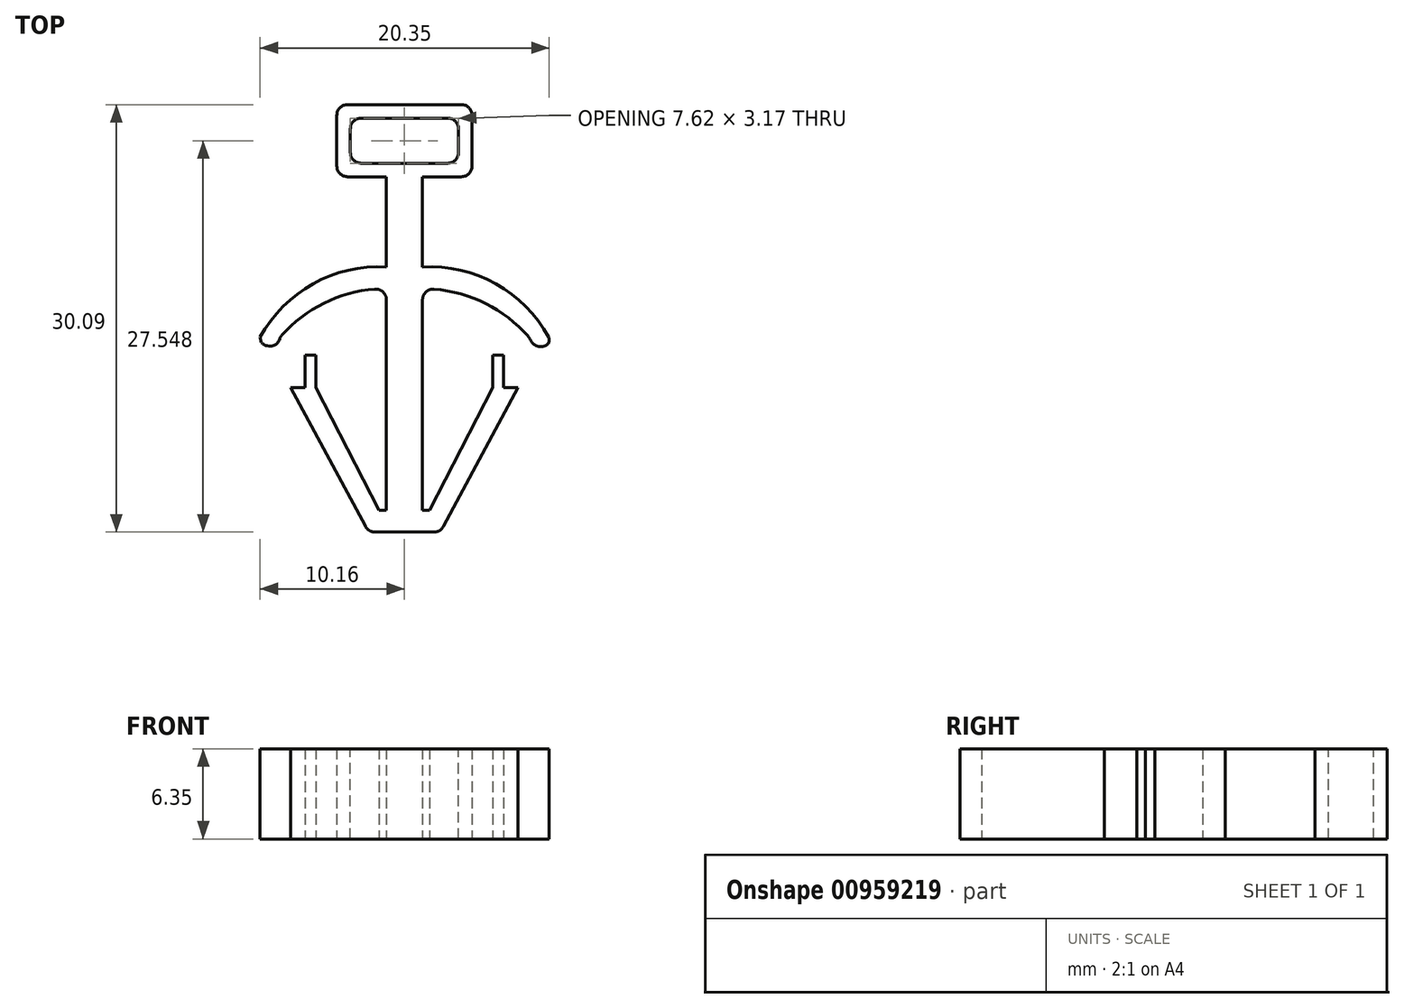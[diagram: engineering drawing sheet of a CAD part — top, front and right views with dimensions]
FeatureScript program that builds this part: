
annotation { "Feature Type Name" : "Feature", "Feature Type Description" : "" }
export const myFeature = defineFeature(function(context is Context, id is Id, definition is map)
    precondition{}
    {
        {
            var Q0;
            Q0=qCreatedBy(makeId("Top.planeOp"),FACE);
            var sketch = newSketch(context, id + "F0", { "sketchPlane" : qUnion([Q0])});
            skLineSegment(sketch, "E0", {"start": v(-4.76, 16.37) * mm, "end": v(4.76, 16.37) * mm});
            skLineSegment(sketch, "E1", {"start": v(4.76, 16.37) * mm, "end": v(4.76, 11.29) * mm});
            skLineSegment(sketch, "E2", {"start": v(4.76, 11.29) * mm, "end": v(1.27, 11.29) * mm});
            skLineSegment(sketch, "E3", {"start": v(1.27, 11.29) * mm, "end": v(1.27, 4.94) * mm});
            skLineSegment(sketch, "E4", {"start": v(-4.76, 16.37) * mm, "end": v(-4.76, 11.29) * mm});
            skLineSegment(sketch, "E5", {"start": v(-4.76, 11.29) * mm, "end": v(-1.27, 11.29) * mm});
            skLineSegment(sketch, "E6", {"start": v(-1.27, 11.29) * mm, "end": v(-1.27, 4.94) * mm});
            skArc(sketch, "E7", {"start": v(10.16, 0) * mm, "mid": v(6.43, 3.75) * mm, "end": v(1.27, 4.94) * mm});
            skArc(sketch, "E8", {"start": v(-1.27, 4.94) * mm, "mid": v(-6.43, 3.75) * mm, "end": v(-10.16, 0) * mm});
            skPoint(sketch, "E9", {"position": v(0, 16.37) * mm});
            skLineSegment(sketch, "E10", {"start": v(-1.8, -4.57) * mm, "end": v(1.8, -4.57) * mm, "construction": true});
            skPoint(sketch, "E11", {"position": v(0, -4.57) * mm});
            skLineSegment(sketch, "E12", {"start": v(-1.27, 11.29) * mm, "end": v(1.27, 11.29) * mm, "construction": true});
            skPoint(sketch, "E13", {"position": v(0, 11.29) * mm});
            skArc(sketch, "E14", {"start": v(-1.27, 3.41) * mm, "mid": v(-5.38, 2.52) * mm, "end": v(-8.75, 0) * mm});
            skArc(sketch, "E15", {"start": v(8.75, 0) * mm, "mid": v(5.38, 2.52) * mm, "end": v(1.27, 3.41) * mm});
            skLineSegment(sketch, "E16", {"start": v(-1.27, 4.94) * mm, "end": v(-1.27, 3.41) * mm, "construction": true});
            skLineSegment(sketch, "E17", {"start": v(-1.27, -12.2) * mm, "end": v(-1.78, -12.2) * mm});
            skLineSegment(sketch, "E18", {"start": v(-1.78, -12.2) * mm, "end": v(-6.22, -3.56) * mm});
            skLineSegment(sketch, "E19", {"start": v(-6.22, -3.56) * mm, "end": v(-6.22, -1.27) * mm});
            skLineSegment(sketch, "E20", {"start": v(-6.22, -1.27) * mm, "end": v(-6.99, -1.27) * mm});
            skLineSegment(sketch, "E21", {"start": v(-6.99, -1.27) * mm, "end": v(-6.99, -3.56) * mm});
            skLineSegment(sketch, "E22", {"start": v(-6.99, -3.56) * mm, "end": v(-8, -3.56) * mm});
            skLineSegment(sketch, "E23", {"start": v(-8, -3.56) * mm, "end": v(-2.54, -13.72) * mm});
            skLineSegment(sketch, "E24", {"start": v(2.54, -13.72) * mm, "end": v(8, -3.56) * mm});
            skLineSegment(sketch, "E25", {"start": v(8, -3.56) * mm, "end": v(6.99, -3.56) * mm});
            skLineSegment(sketch, "E26", {"start": v(6.99, -3.56) * mm, "end": v(6.99, -1.27) * mm});
            skLineSegment(sketch, "E27", {"start": v(6.99, -1.27) * mm, "end": v(6.22, -1.27) * mm});
            skLineSegment(sketch, "E28", {"start": v(1.27, -12.2) * mm, "end": v(1.27, 3.41) * mm});
            skLineSegment(sketch, "E29", {"start": v(6.22, -1.27) * mm, "end": v(6.22, -3.56) * mm});
            skLineSegment(sketch, "E30", {"start": v(6.22, -3.56) * mm, "end": v(1.78, -12.2) * mm});
            skLineSegment(sketch, "E31", {"start": v(1.27, -12.2) * mm, "end": v(1.78, -12.2) * mm});
            skPoint(sketch, "E32", {"position": v(0, -10.6) * mm});
            skLineSegment(sketch, "E33", {"start": v(-1.27, 3.41) * mm, "end": v(-1.27, -12.2) * mm});
            skLineSegment(sketch, "E34", {"start": v(-1.27, -6.5) * mm, "end": v(1.27, -6.5) * mm, "construction": true});
            skPoint(sketch, "E35", {"position": v(0, -6.5) * mm});
            skLineSegment(sketch, "E36", {"start": v(-6.22, -1.27) * mm, "end": v(6.22, -1.27) * mm, "construction": true});
            skPoint(sketch, "E37", {"position": v(0, -1.27) * mm});
            skLineSegment(sketch, "E38", {"start": v(-2.54, -13.72) * mm, "end": v(2.54, -13.72) * mm});
            skFitSpline(sketch, "E39", {"points": [v(8.75, 0) * mm, v(9.19, -0.56) * mm, v(9.96, -0.6) * mm, v(10.16, 0) * mm], "startDerivative": vector(1.13, -1.86) * mm, "endDerivative": vector(-0.7, 2.78) * mm});
            skFitSpline(sketch, "E40", {"points": [v(-8.75, 0) * mm, v(-9.15, -0.57) * mm, v(-9.97, -0.48) * mm, v(-10.16, 0) * mm], "startDerivative": vector(-0.5, -2.14) * mm, "endDerivative": vector(-0.23, 2.02) * mm});
            skSolve(sketch);
        }
        {
            var Q0;
            Q0 = qSketchRegion(id + "F0", true);
            extrude(context, id + "F1", {"entities" : qUnion([Q0]), "depth" : 6.35 * mm, "offsetDistance" : 25.4 * mm});
        }
        {
            var Q0;
            Q0=makeQuery(id+"F1.opExtrude","SWEPT_EDGE",EDGE,{"disambiguationData":[OSD([sQuery(id+"F0.wireOp",EDGE,"E23"),sQuery(id+"F0.wireOp",EDGE,"E38")])]});
            var Q1;
            Q1=makeQuery(id+"F1.opExtrude","SWEPT_EDGE",EDGE,{"disambiguationData":[OSD([sQuery(id+"F0.wireOp",EDGE,"E24"),sQuery(id+"F0.wireOp",EDGE,"E38")])]});
            var Q2;
            Q2=makeQuery(id+"F1.opExtrude","SWEPT_EDGE",EDGE,{"disambiguationData":[OSD([sQuery(id+"F0.wireOp",EDGE,"E0"),sQuery(id+"F0.wireOp",EDGE,"E4")])]});
            var Q3;
            Q3=makeQuery(id+"F1.opExtrude","SWEPT_EDGE",EDGE,{"disambiguationData":[OSD([sQuery(id+"F0.wireOp",EDGE,"E4"),sQuery(id+"F0.wireOp",EDGE,"E5")])]});
            var Q4;
            Q4=makeQuery(id+"F1.opExtrude","SWEPT_EDGE",EDGE,{"disambiguationData":[OSD([sQuery(id+"F0.wireOp",EDGE,"E0"),sQuery(id+"F0.wireOp",EDGE,"E1")])]});
            var Q5;
            Q5=makeQuery(id+"F1.opExtrude","SWEPT_EDGE",EDGE,{"disambiguationData":[OSD([sQuery(id+"F0.wireOp",EDGE,"E1"),sQuery(id+"F0.wireOp",EDGE,"E2")])]});
            var Q6;
            Q6=makeQuery(id+"F1.opExtrude","SWEPT_EDGE",EDGE,{"disambiguationData":[OSD([sQuery(id+"F0.wireOp",EDGE,"uqZX6xxm-t7tZ-jXcq-WQOi-cOfuqDcAQbNt"),sQuery(id+"F0.wireOp",EDGE,"E14")])]});
            var Q7;
            Q7=makeQuery(id+"F1.opExtrude","SWEPT_EDGE",EDGE,{"disambiguationData":[OSD([sQuery(id+"F0.wireOp",EDGE,"NnzWqAFU-uv6o-BWG9-L6w1-fhSG610Yaf7F"),sQuery(id+"F0.wireOp",EDGE,"E15")])]});
            fillet(context, id + "F2", {"entities" : qUnion([Q0, Q1, Q2, Q3, Q4, Q5, Q6, Q7]), "radius" : 0.76 * mm, "tangentPropagation" : true, "allowEdgeOverflow" : false});
        }
        {
            var Q0;
            Q0=makeQuery(id+"F1.opExtrude","CAP_FACE",FACE,{"disambiguationData":[OSD([sQuery(id+"F0.wireOp",EDGE,"E0"),sQuery(id+"F0.wireOp",EDGE,"E1"),sQuery(id+"F0.wireOp",EDGE,"E2"),sQuery(id+"F0.wireOp",EDGE,"E3"),sQuery(id+"F0.wireOp",EDGE,"E4"),sQuery(id+"F0.wireOp",EDGE,"E5"),sQuery(id+"F0.wireOp",EDGE,"E6"),sQuery(id+"F0.wireOp",EDGE,"E7"),sQuery(id+"F0.wireOp",EDGE,"E8"),sQuery(id+"F0.wireOp",EDGE,"uqZX6xxm-t7tZ-jXcq-WQOi-cOfuqDcAQbNt"),sQuery(id+"F0.wireOp",EDGE,"NnzWqAFU-uv6o-BWG9-L6w1-fhSG610Yaf7F"),sQuery(id+"F0.wireOp",EDGE,"E14"),sQuery(id+"F0.wireOp",EDGE,"E15"),sQuery(id+"F0.wireOp",EDGE,"E17"),sQuery(id+"F0.wireOp",EDGE,"E18"),sQuery(id+"F0.wireOp",EDGE,"E19"),sQuery(id+"F0.wireOp",EDGE,"E20"),sQuery(id+"F0.wireOp",EDGE,"E21"),sQuery(id+"F0.wireOp",EDGE,"E22"),sQuery(id+"F0.wireOp",EDGE,"E23"),sQuery(id+"F0.wireOp",EDGE,"E24"),sQuery(id+"F0.wireOp",EDGE,"E25"),sQuery(id+"F0.wireOp",EDGE,"E26"),sQuery(id+"F0.wireOp",EDGE,"E27"),sQuery(id+"F0.wireOp",EDGE,"E28"),sQuery(id+"F0.wireOp",EDGE,"E29"),sQuery(id+"F0.wireOp",EDGE,"E30"),sQuery(id+"F0.wireOp",EDGE,"E31"),sQuery(id+"F0.wireOp",EDGE,"E33"),sQuery(id+"F0.wireOp",EDGE,"E38")])],"isStart":false});
            var sketch = newSketch(context, id + "F3", { "sketchPlane" : qUnion([Q0])});
            skLineSegment(sketch, "E41.bottom", {"start": v(3.05, 12.24) * mm, "end": v(-3.05, 12.24) * mm});
            skLineSegment(sketch, "E41.top", {"start": v(3.05, 15.42) * mm, "end": v(-3.05, 15.42) * mm});
            skLineSegment(sketch, "E41.left", {"start": v(3.81, 13) * mm, "end": v(3.81, 14.65) * mm});
            skLineSegment(sketch, "E41.right", {"start": v(-3.8, 13) * mm, "end": v(-3.8, 14.65) * mm});
            skPoint(sketch, "E41.middle", {"position": v(0, 13.83) * mm});
            skLineSegment(sketch, "E42", {"start": v(-2, 11.29) * mm, "end": v(-2, 12.24) * mm, "construction": true});
            skLineSegment(sketch, "E43", {"start": v(-2, 16.37) * mm, "end": v(-2, 15.42) * mm, "construction": true});
            skPoint(sketch, "E44.visualSharp", {"position": v(-3.8, 15.42) * mm});
            skArc(sketch, "E44.filletArc", {"start": v(-3.05, 15.42) * mm, "mid": v(-3.59, 15.2) * mm, "end": v(-3.8, 14.65) * mm});
            skPoint(sketch, "E45.visualSharp", {"position": v(-3.8, 12.24) * mm});
            skArc(sketch, "E45.filletArc", {"start": v(-3.8, 13) * mm, "mid": v(-3.59, 12.46) * mm, "end": v(-3.05, 12.24) * mm});
            skPoint(sketch, "E46.visualSharp", {"position": v(3.81, 12.24) * mm});
            skArc(sketch, "E46.filletArc", {"start": v(3.05, 12.24) * mm, "mid": v(3.59, 12.46) * mm, "end": v(3.81, 13) * mm});
            skPoint(sketch, "E47.visualSharp", {"position": v(3.81, 15.42) * mm});
            skArc(sketch, "E47.filletArc", {"start": v(3.81, 14.65) * mm, "mid": v(3.59, 15.2) * mm, "end": v(3.05, 15.42) * mm});
            skSolve(sketch);
        }
        {
            var Q0;
            Q0 = qSketchRegion(id + "F3", true);
            extrude(context, id + "F4", {"entities" : qUnion([Q0]), "operationType" : NewBodyOperationType.REMOVE, "endBound" : BoundingType.THROUGH_ALL, "oppositeDirection" : true, "depth" : 25.4 * mm, "offsetDistance" : 25.4 * mm});
        }
    });
